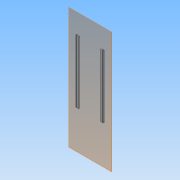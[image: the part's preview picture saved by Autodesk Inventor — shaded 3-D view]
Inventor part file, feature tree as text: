
AUTODESK INVENTOR PART (.ipt)
format: ipt  version: 2013 (Build 170138000, 138)  size: 112,128 bytes
history: native  units: in
note: dims shown in document units (in); Inventor stores cm internally (conversion verified against a paired STEP export)
features: extrude x2, sketch x2, reference x2, plane x1, projected_geometry x1
ambient origin geometry x8: Origin, YZ Plane, XZ Plane, XY Plane, X Axis, Y Axis, Z Axis, Center Point
bodies: Solid1 (feature_tree)
feature tree (8):
  plane  "Work Plane1"
  extrude  "Extrusion1"  Depth=0.75in TaperAngle=0.0deg
  extrude  "Extrusion2"  Depth=0.5in
  sketch  "Sketch1"  dims[d1=2.5in d2=0.75in d3=0.0in]
  reference  "Reference1"
  reference  "Reference2"
  sketch  "Sketch2"  dims[d5=0.48in d6=0.5in d7=0.5in d8=0.5in d9=0.0in]
  projected_geometry  "Projected Loop1"
